# Revit family: Haworth_ComposeEcho_AccessoryFrame
name_source: partatom
category: Furniture Systems
units: mm (PartAtom-declared; Revit-internal decimal feet)

## family parameters
Always vertical = Yes
Cut with Voids When Loaded = No
OmniClass Number = 23.40.70.14.64.21
OmniClass Title = Systems Furniture
Part Type = Normal
Room Calculation Point = No
Round Connector Dimension = Use Diameter
Shared = No
Work Plane-Based = No

## types (11) — shared parameters
Actual Height = 16 "
Assembly Code = E2020500
Available Heights = 16, 19, 20, 24, and 27 in.
Available Widths = 24-84 in. @ 6in. increments
Description = Haworth - Compose Echo - Accessory Frame
Manufacturer = Haworth
Model = Haworth - Compose Echo
Rail Height = 13.642 "
Revision Number = 1
Screen Height - 12 in = No
Screen Height - 16 in. = Yes
Screen Height - 19 in. = No
Screen Height - 20 in. = No
Screen Height - 24 in. = No
Screen Height - 27 in. = No
Size = Verify Final Dim. w/ Haworth
Sustainability Info = https://library.haworth.com
URL = www.haworth.com
URL - Product = http://www.haworth.com
Warranty = http://www.haworth.com

## per-type parameters (varying)
| type | Actual Width | Half Rail Width | Rail Width |
| 24w 16h | 24 " | 5 " | 10 " |
| 30w 16h | 30 " | 8 " | 16 " |
| 36w 16h | 36 " | 11 " | 22 " |
| 42w 16h | 42 " | 14 " | 28 " |
| 48w 16h | 48 " | 17 " | 34 " |
| 54w 16h | 54 " | 20 " | 40 " |
| 60w 16h | 60 " | 23 " | 46 " |
| 66w 16h | 66 " | 26 " | 52 " |
| 72w 16h | 72 " | 29 " | 58 " |
| 78w 16h | 78 " | 32 " | 64 " |
| 84w 16h | 84 " | 35 " | 70 " |

## geometry (parser evidence)
native form markers: Sweep x24
no freeform markers — native parametric forms only
